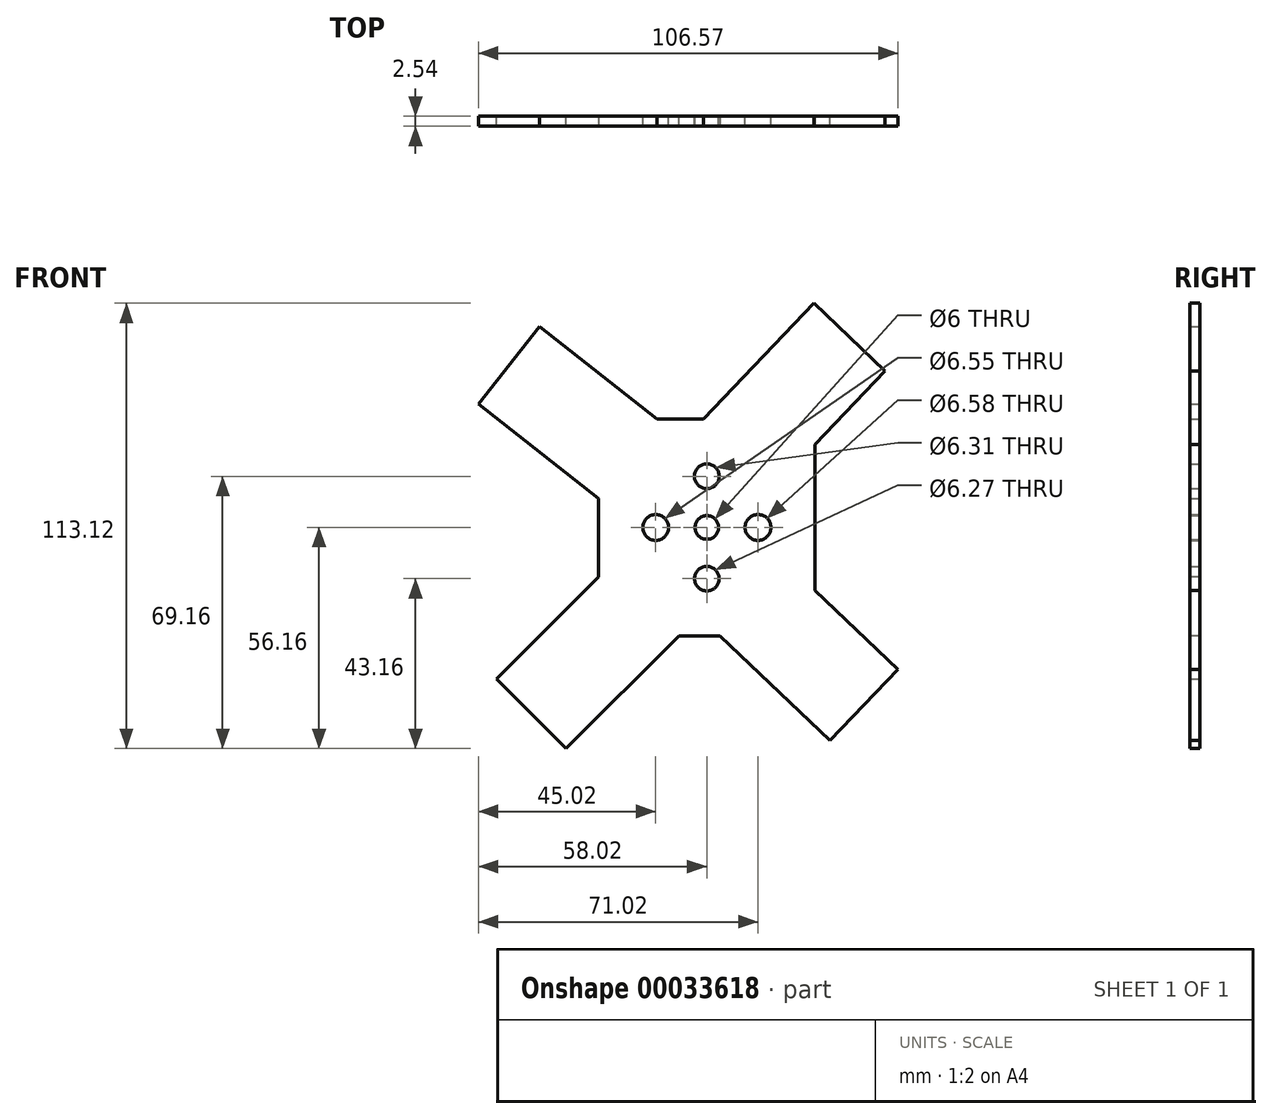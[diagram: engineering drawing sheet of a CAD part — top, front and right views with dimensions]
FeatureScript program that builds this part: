
annotation { "Feature Type Name" : "Feature", "Feature Type Description" : "" }
export const myFeature = defineFeature(function(context is Context, id is Id, definition is map)
    precondition{}
    {
        {
            var Q0;
            Q0=qCreatedBy(makeId("Front.planeOp"),FACE);
            var sketch = newSketch(context, id + "F0", { "sketchPlane" : qUnion([Q0])});
            skLineSegment(sketch, "E0.rect.bottom", {"start": v(27.5, -27.5) * mm, "end": v(-27.5, -27.5) * mm});
            skLineSegment(sketch, "E0.rect.top", {"start": v(27.5, 27.5) * mm, "end": v(-27.5, 27.5) * mm});
            skLineSegment(sketch, "E0.rect.left", {"start": v(27.5, -27.5) * mm, "end": v(27.5, 27.5) * mm});
            skLineSegment(sketch, "E0.rect.right", {"start": v(-27.5, -27.5) * mm, "end": v(-27.5, 27.5) * mm});
            skPoint(sketch, "E0.rect.middle", {"position": v(0, 0) * mm});
            skCircle(sketch, "E1", {"center": v(0, 0) * mm, "radius": 3 * mm});
            skCircle(sketch, "E2", {"center": v(-13, 0) * mm, "radius": 3.27 * mm});
            skCircle(sketch, "E3", {"center": v(13, 0) * mm, "radius": 3.3 * mm});
            skCircle(sketch, "E4", {"center": v(0, 13) * mm, "radius": 3.16 * mm});
            skCircle(sketch, "E5", {"center": v(0, -13) * mm, "radius": 3.13 * mm});
            skSolve(sketch);
        }
        {
            var Q0;
            Q0=makeQuery(id+"F0.imprint","IMPRINT",FACE,{"disambiguationData":[TD([[makeQuery(id+"F0.imprint","IMPRINT",EDGE,{"derivedFrom":sQuery(id+"F0.wireOp",EDGE,"E0.rect.bottom")}),-1.0]])]});
            extrude(context, id + "F1", {"entities" : qUnion([Q0]), "depth" : 2.54 * mm});
        }
        {
            var Q0;
            Q0=qCreatedBy(makeId("Front.planeOp"),FACE);
            var sketch = newSketch(context, id + "F2", { "sketchPlane" : qUnion([Q0])});
            skLineSegment(sketch, "E6", {"start": v(-2.27, 26) * mm, "end": v(27.18, 56.96) * mm});
            skLineSegment(sketch, "E7", {"start": v(27.18, 56.96) * mm, "end": v(45.29, 39.73) * mm});
            skLineSegment(sketch, "E8", {"start": v(45.29, 39.73) * mm, "end": v(15.79, 8.72) * mm});
            skLineSegment(sketch, "E9", {"start": v(15.79, 8.72) * mm, "end": v(-2.27, 25.9) * mm});
            skLineSegment(sketch, "E10", {"start": v(-2.27, 25.9) * mm, "end": v(-2.27, 26) * mm});
            skPoint(sketch, "E11", {"position": v(4.42, 33.04) * mm});
            skPoint(sketch, "E12", {"position": v(19.52, 12.64) * mm});
            skLineSegment(sketch, "E13", {"start": v(-10.96, 26.18) * mm, "end": v(-42.57, 51.02) * mm});
            skLineSegment(sketch, "E14", {"start": v(-42.57, 51.02) * mm, "end": v(-58.02, 31.37) * mm});
            skLineSegment(sketch, "E15", {"start": v(-58.02, 31.37) * mm, "end": v(-26.06, 6.25) * mm});
            skLineSegment(sketch, "E16", {"start": v(-26.06, 6.25) * mm, "end": v(-10.96, 26.18) * mm});
            skLineSegment(sketch, "E17", {"start": v(-23.23, -8.27) * mm, "end": v(-53.44, -38.48) * mm});
            skLineSegment(sketch, "E18", {"start": v(-53.44, -38.48) * mm, "end": v(-35.76, -56.16) * mm});
            skLineSegment(sketch, "E19", {"start": v(-35.76, -56.16) * mm, "end": v(-5.33, -25.73) * mm});
            skLineSegment(sketch, "E20", {"start": v(-5.33, -25.73) * mm, "end": v(-23.23, -8.27) * mm});
            skLineSegment(sketch, "E21", {"start": v(2.62, -26.83) * mm, "end": v(31.32, -54.13) * mm});
            skLineSegment(sketch, "E22", {"start": v(31.32, -54.13) * mm, "end": v(48.55, -36.02) * mm});
            skLineSegment(sketch, "E23", {"start": v(48.55, -36.02) * mm, "end": v(19.7, -8.57) * mm});
            skLineSegment(sketch, "E24", {"start": v(19.7, -8.57) * mm, "end": v(2.62, -26.83) * mm});
            skPoint(sketch, "E25", {"position": v(-27.54, -12.58) * mm});
            skPoint(sketch, "E26", {"position": v(-27.54, 7.42) * mm});
            skPoint(sketch, "E27", {"position": v(-15.58, 29.81) * mm});
            skPoint(sketch, "E28", {"position": v(-7.1, -27.5) * mm});
            skPoint(sketch, "E29", {"position": v(18.42, -7.36) * mm});
            skPoint(sketch, "E30", {"position": v(11.38, -35.16) * mm});
            skSolve(sketch);
        }
        {
            var Q0;
            {var subQ4=sQuery(id+"F2.wireOp",EDGE,"E7");Q0=makeQuery(id+"F2.imprint","IMPRINT",FACE,{"disambiguationData":[TD([[makeQuery(id+"F2.imprint","IMPRINT",EDGE,{"derivedFrom":subQ4}),-1.0]])]});}
            extrude(context, id + "F3", {"entities" : qUnion([Q0]), "operationType" : NewBodyOperationType.ADD, "depth" : 2.54 * mm});
        }
        {
            var Q0;
            Q0=makeQuery(id+"F2.imprint","IMPRINT",FACE,{"disambiguationData":[TD([[makeQuery(id+"F2.imprint","IMPRINT",EDGE,{"derivedFrom":sQuery(id+"F2.wireOp",EDGE,"E17")}),1.0]])]});
            var Q1;
            Q1=makeQuery(id+"F2.imprint","IMPRINT",FACE,{"disambiguationData":[TD([[makeQuery(id+"F2.imprint","IMPRINT",EDGE,{"derivedFrom":sQuery(id+"F2.wireOp",EDGE,"E21")}),1.0]])]});
            var Q2;
            Q2=makeQuery(id+"F2.imprint","IMPRINT",FACE,{"disambiguationData":[TD([[makeQuery(id+"F2.imprint","IMPRINT",EDGE,{"derivedFrom":sQuery(id+"F2.wireOp",EDGE,"E13")}),1.0]])]});
            extrude(context, id + "F4", {"entities" : qUnion([Q0, Q1, Q2]), "operationType" : NewBodyOperationType.ADD, "depth" : 2.54 * mm});
        }
    });
